# Revit family: PRD_AR_ShwrThrmsttcVlvs_ThermostaticSingle-leverWall-mountedMixer_F5LT2001_F5LT2003
name_source: partatom
category: Plumbing Fixtures
units: mm (PartAtom-declared; Revit-internal decimal feet)

## family parameters
Cut with Voids When Loaded = Yes
Host = Face
OmniClass Number = 23.45.55.17
OmniClass Title = Mixing Faucets
Part Type = Normal
Room Calculation Point = No
Round Connector Dimension = Use Diameter
Shared = No

## types (2) — shared parameters
AccentColour = none
AdditionalConnections = no
AssetType = Fixed
BasicColour = chrome-look (glossy)
BodyMaterial = PRD_AR_ChromatedBrass_HighPolished
Category = Pr_40_20_87_80, Shower thermostatic valves
Circulation = no
CloseOffRating = 0.0 Pa
Color = chrome-look (glossy)
ConnectionWithPayWaterDispenser = not possible
Default Elevation = 1219 mm
DiameterNominal = 15  [stored 0.0492126 ft]
DurationUnit = year
Finish = polished chrome-plated
FunctionalPrinciple = manual
HygieneFlushing = prepared
IfcExportAs = IfcValveType
IfcExportType = MIXING
InletSize = G 1/2 B
LockingMechanism = Top section, ceramic
Manufacturer = KWC Group AG
ManufacturerName = KWC Group AG
ManufacturerURL = www.kwc.com
Material = Brass
MaterialCasing = brass-look
MaterialFitting = brass-look
MinimumFlowPressure = 1 bar
MixerControl = OTHER
NBSDescription = Shower mixers
NBSReference = 45-35-70/335
NominalDepth = 140 mm  [stored 0.459318 ft]
NominalWidth = 288 mm  [stored 0.944882 ft]
PositionOfWaterConnection = from backside
ProductInformation = http://pim.kwc.com
ProtectiveShutdown = no
Shape = Bib tap
ShowerPipeDraining = no
Size = 15
SoundInsulation = no
Status = New
SurfaceFinishCasing = chromed
SurfaceFinishFitting = chromed
SurfaceTreatmentFitting = polished
TailorMade = no
TemperatureLimit = yes
TestPressure = 0.0 Pa
ThermalDisinfection = yes
TypeOfMixing = with thermostat
TypeOfMounting = wall mounting
TypeOfOperation = manual operation
TypeOfShower = wall fitting
URL = www.kwc.com
Uniclass2015Code = Pr_40_20_87_80
Uniclass2015Title = Shower thermostatic valves
Uniclass2015Version = Products v1.32
ValveMechanism = OTHER
ValveOperation = OTHER
ValvePattern = ANGLED_2_PORT
Version = 1
VolumeFlowRate = 0.25 l/s at 3 bar
WarrantyDurationUnit = year
WaterConnection = S-unions
WithBackflowPreventer = yes
WithFilter = yes
WithRosettesOrCoverPlate = yes
WorkingPressure = 0.0 Pa
zero-valued in all types: FlowCoefficient, NominalHeight

## per-type parameters (varying)
| type | BIMObjectName | ConnectorMovement | Description | F5LT2001 | F5LT2003 | Features | ForHandShower | ModelNumber | Name | OutletConnectionSize |
| F5LT2001 | PRD_AR_ShowerThermostaticValves_ThermostaticSingle-leverWall-mountedMixer_F5LT2001 | 5 mm  [stored 0.0164042 ft] | F5L-Therm thermostatic single-lever mixer as DN 15 wall-mounted mixer for wall mounting, for shower facilities. Thermostatically-controlled mixer cartridge with expansion element and active scald protection as well as adjustable and turn-proof temperature stop, and ceramic disc technology. With mechanism for optional hygiene unit for automatic hygiene flushing, program-controlled thermal disinfection (additional bypass solenoid-operated flush valve cartridge necessary) and storage of statistical data. For connection to hot and cold water. Scald-protection Safe-Touch housing with outlet on top, G 3/4 B, for installation of waste elbow or wall-mounted shower pipe. All-metal construction, high-polished chrome-plated brass. With adjustable and lockable connections with backflow preventers and strainers, fully covered by depth-adjustable screw rosettes. | Yes | No | For connection to hot water and cold water. Outlet on top. | no | 2030066495 | F5L-Therm thermostatic single-lever wall-mounted mixer F5LT2001 | 20 mm  [stored 0.0656168 ft] |
| F5LT2003 | PRD_AR_ShowerThermostaticValves_ThermostaticSingle-leverWall-mountedMixer_F5LT2003 | 91 mm  [stored 0.298556 ft] | F5L-Therm thermostatic single-lever mixer as DN 15 wall-mounted mixer for wall mounting, for shower facilities. Thermostatically-controlled mixer cartridge with expansion element and active scald protection as well as adjustable and turn-proof temperature stop, and ceramic disc technology. With mechanism for optional hygiene unit for automatic hygiene flushing, program-controlled thermal disinfection (additional bypass solenoid-operated flush valve cartridge necessary) and storage of statistical data. For connection to hot and cold water. Scald-protection, Safe-Touch housing with hand shower connection, G 1/2 B. All-metal construction, high-polished chrome-plated brass. With adjustable and lockable connections with backflow preventers and strainers, fully covered by depth-adjustable screw rosettes. | No | Yes | For connection to hot water and cold water. With hand shower connection. | yes | 2030066497 | F5L-Therm thermostatic single-lever wall-mounted mixer with hand shower connection F5LT2003 | 15 mm  [stored 0.0492126 ft] |

note: column(s) folded — value = type name in every type: Model, ModelReference

note: [stored X ft] marks values corroborated as IEEE doubles in the binary element streams (Revit-internal decimal feet)

## geometry (parser evidence)
native form markers: Sweep x8
no freeform markers — native parametric forms only
